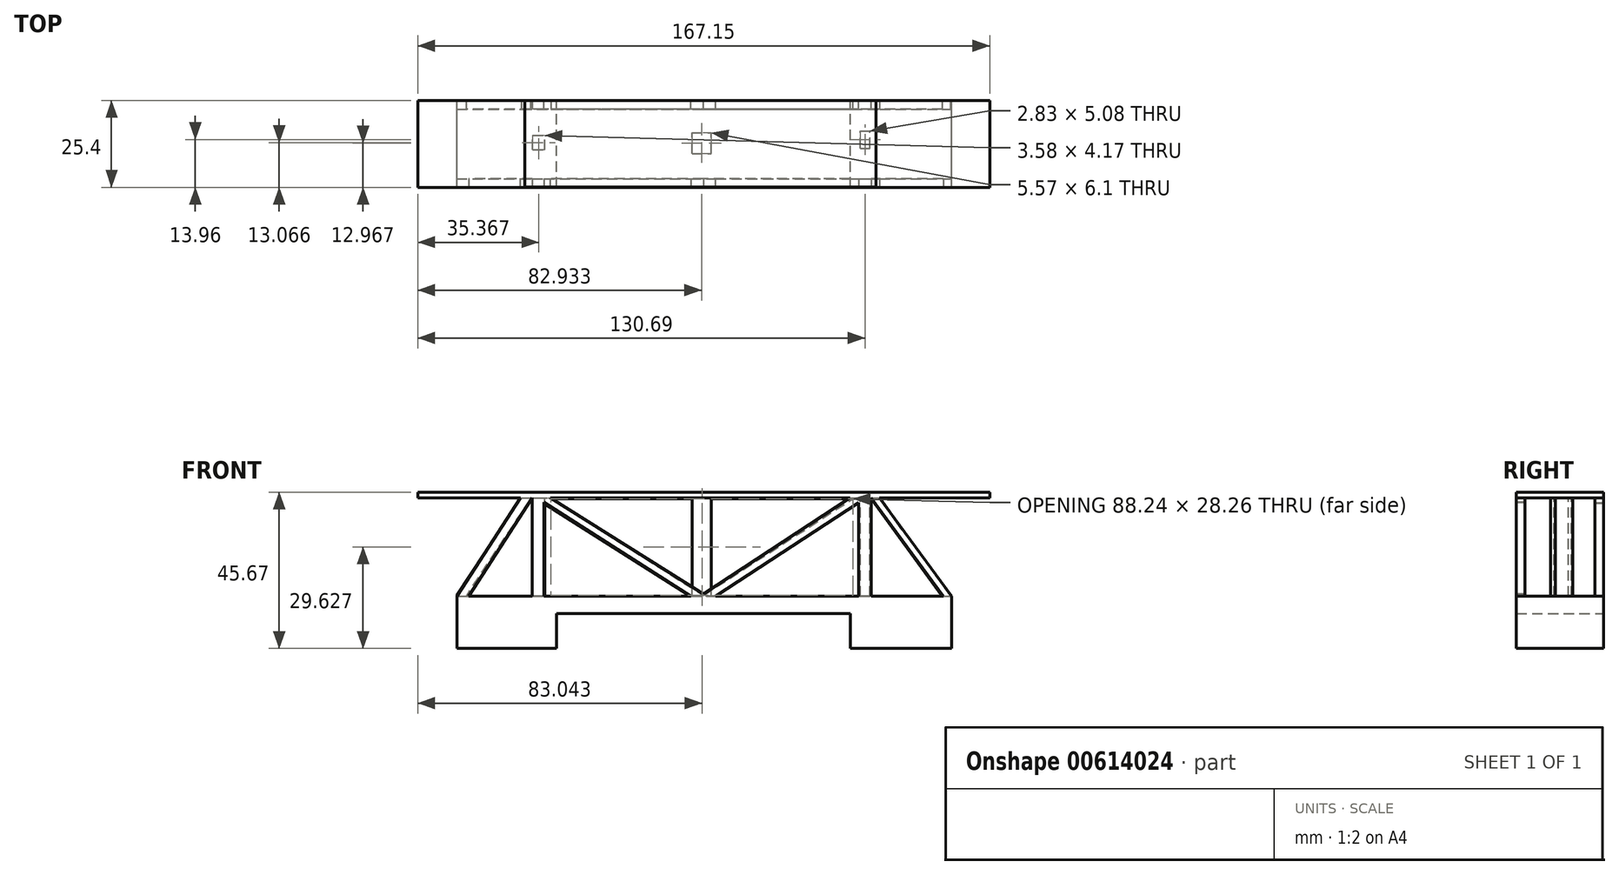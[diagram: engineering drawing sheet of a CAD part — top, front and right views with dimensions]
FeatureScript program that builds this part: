
annotation { "Feature Type Name" : "Feature", "Feature Type Description" : "" }
export const myFeature = defineFeature(function(context is Context, id is Id, definition is map)
    precondition{}
    {
        {
            var Q0;
            Q0=qCreatedBy(makeId("Front.planeOp"),FACE);
            var sketch = newSketch(context, id + "F0", { "sketchPlane" : qUnion([Q0])});
            skLineSegment(sketch, "E0.bottom", {"start": v(-72.04, 2.38) * mm, "end": v(72.6, 2.38) * mm});
            skLineSegment(sketch, "E0.top", {"start": v(-72.04, -2.66) * mm, "end": v(72.6, -2.66) * mm});
            skLineSegment(sketch, "E0.left", {"start": v(-72.04, 2.38) * mm, "end": v(-72.04, -2.66) * mm});
            skLineSegment(sketch, "E0.right", {"start": v(72.6, 2.38) * mm, "end": v(72.6, -2.66) * mm});
            skSolve(sketch);
        }
        {
            var Q0;
            Q0 = qSketchRegion(id + "F0", true);
            extrude(context, id + "F1", {"entities" : qUnion([Q0]), "depth" : 25.4 * mm, "offsetDistance" : 25.4 * mm});
        }
        {
            var Q0;
            Q0=qCreatedBy(makeId("Front.planeOp"),FACE);
            var sketch = newSketch(context, id + "F2", { "sketchPlane" : qUnion([Q0])});
            skLineSegment(sketch, "E1", {"start": v(-72.04, 0) * mm, "end": v(-72.04, 2.66) * mm});
            skLineSegment(sketch, "E2", {"start": v(-72.04, 2.66) * mm, "end": v(-52.17, 32.6) * mm});
            skLineSegment(sketch, "E3", {"start": v(-52.17, 32.6) * mm, "end": v(50.5, 32.6) * mm});
            skLineSegment(sketch, "E4", {"start": v(50.5, 32.6) * mm, "end": v(72.33, 2.35) * mm});
            skLineSegment(sketch, "E5", {"start": v(72.33, 2.35) * mm, "end": v(72.33, 0) * mm});
            skLineSegment(sketch, "E6", {"start": v(72.33, 0) * mm, "end": v(69.99, 0) * mm});
            skLineSegment(sketch, "E7", {"start": v(69.99, 0) * mm, "end": v(69.99, 2.13) * mm});
            skLineSegment(sketch, "E8", {"start": v(69.99, 2.13) * mm, "end": v(49, 30.94) * mm});
            skLineSegment(sketch, "E9", {"start": v(49, 30.94) * mm, "end": v(-50.44, 30.94) * mm});
            skLineSegment(sketch, "E10", {"start": v(-50.44, 30.94) * mm, "end": v(-69.24, 2.6) * mm});
            skLineSegment(sketch, "E11", {"start": v(-69.24, 2.6) * mm, "end": v(-69.24, 0) * mm});
            skLineSegment(sketch, "E12", {"start": v(-69.24, 0) * mm, "end": v(-72.04, 0) * mm});
            skSolve(sketch);
        }
        {
            var Q0;
            Q0 = qSketchRegion(id + "F2", true);
            extrude(context, id + "F3", {"entities" : qUnion([Q0]), "operationType" : NewBodyOperationType.ADD, "depth" : 2.54 * mm, "offsetDistance" : 25.4 * mm});
        }
        {
            var Q0;
            Q0=makeQuery(id+"F1.opExtrude","CAP_FACE",FACE,{"disambiguationData":[OSD([sQuery(id+"F0.wireOp",EDGE,"E0.bottom"),sQuery(id+"F0.wireOp",EDGE,"E0.top"),sQuery(id+"F0.wireOp",EDGE,"E0.left"),sQuery(id+"F0.wireOp",EDGE,"E0.right")])],"isStart":false});
            var sketch = newSketch(context, id + "F4", { "sketchPlane" : qUnion([Q0])});
            skLineSegment(sketch, "E13", {"start": v(-72.04, -0.14) * mm, "end": v(-72.04, 2.38) * mm});
            skLineSegment(sketch, "E14", {"start": v(-72.04, 2.38) * mm, "end": v(-52.32, 32.77) * mm});
            skLineSegment(sketch, "E15", {"start": v(-52.32, 32.77) * mm, "end": v(50.21, 32.77) * mm});
            skLineSegment(sketch, "E16", {"start": v(50.21, 32.77) * mm, "end": v(72.6, 2.38) * mm});
            skLineSegment(sketch, "E17", {"start": v(72.6, 2.38) * mm, "end": v(72.6, 0) * mm});
            skLineSegment(sketch, "E18", {"start": v(72.6, 0) * mm, "end": v(70.08, 0) * mm});
            skLineSegment(sketch, "E19", {"start": v(70.08, 0) * mm, "end": v(70.08, 2.38) * mm});
            skLineSegment(sketch, "E20", {"start": v(70.08, 2.38) * mm, "end": v(49.03, 31.08) * mm});
            skLineSegment(sketch, "E21", {"start": v(49.03, 31.08) * mm, "end": v(-49.96, 31.08) * mm});
            skLineSegment(sketch, "E22", {"start": v(-49.96, 31.08) * mm, "end": v(-68.59, 2.38) * mm});
            skLineSegment(sketch, "E23", {"start": v(-68.59, 2.38) * mm, "end": v(-68.59, 0) * mm});
            skLineSegment(sketch, "E24", {"start": v(-68.59, 0) * mm, "end": v(-72.04, -0.14) * mm});
            skSolve(sketch);
        }
        {
            var Q0;
            Q0 = qSketchRegion(id + "F4", true);
            extrude(context, id + "F5", {"entities" : qUnion([Q0]), "operationType" : NewBodyOperationType.ADD, "oppositeDirection" : true, "depth" : 2.54 * mm, "offsetDistance" : 25.4 * mm});
        }
        {
            var Q0;
            Q0=makeQuery(id+"F3.opExtrude","SWEPT_FACE",FACE,{"disambiguationData":[OSD([sQuery(id+"F2.wireOp",EDGE,"E3")])]});
            var sketch = newSketch(context, id + "F6", { "sketchPlane" : qUnion([Q0])});
            skLineSegment(sketch, "E25", {"start": v(-52.17, 0) * mm, "end": v(-52.17, -25.28) * mm});
            skLineSegment(sketch, "E26", {"start": v(-52.17, -25.28) * mm, "end": v(50.5, -25.28) * mm});
            skLineSegment(sketch, "E27", {"start": v(50.5, -25.28) * mm, "end": v(50.5, 0) * mm});
            skLineSegment(sketch, "E28", {"start": v(50.5, 0) * mm, "end": v(-52.17, 0) * mm});
            skSolve(sketch);
        }
        {
            var Q0;
            Q0 = qSketchRegion(id + "F6", true);
            extrude(context, id + "F7", {"entities" : qUnion([Q0]), "operationType" : NewBodyOperationType.ADD, "depth" : 0.25 * mm, "offsetDistance" : 25.4 * mm});
        }
        {
            var Q0;
            Q0=makeQuery(id+"F5.boolean.opBoolean","MERGE",FACE,{"derivedFrom":[makeQuery(id+"F1.opExtrude","CAP_FACE",FACE,{"disambiguationData":[OSD([sQuery(id+"F0.wireOp",EDGE,"E0.bottom"),sQuery(id+"F0.wireOp",EDGE,"E0.top"),sQuery(id+"F0.wireOp",EDGE,"E0.left"),sQuery(id+"F0.wireOp",EDGE,"E0.right")])],"isStart":false}),makeQuery(id+"F5.opExtrude","CAP_FACE",FACE,{"disambiguationData":[OSD([sQuery(id+"F4.wireOp",EDGE,"E13"),sQuery(id+"F4.wireOp",EDGE,"E14"),sQuery(id+"F4.wireOp",EDGE,"E15"),sQuery(id+"F4.wireOp",EDGE,"E16"),sQuery(id+"F4.wireOp",EDGE,"E17"),sQuery(id+"F4.wireOp",EDGE,"E18"),sQuery(id+"F4.wireOp",EDGE,"E19"),sQuery(id+"F4.wireOp",EDGE,"E20"),sQuery(id+"F4.wireOp",EDGE,"E21"),sQuery(id+"F4.wireOp",EDGE,"E22"),sQuery(id+"F4.wireOp",EDGE,"E23"),sQuery(id+"F4.wireOp",EDGE,"E24")])],"isStart":true})]});
            var sketch = newSketch(context, id + "F8", { "sketchPlane" : qUnion([Q0])});
            skLineSegment(sketch, "E29.bottom", {"start": v(-49.96, 31.99) * mm, "end": v(-46.53, 31.99) * mm});
            skLineSegment(sketch, "E29.top", {"start": v(-49.96, 1.21) * mm, "end": v(-46.53, 1.21) * mm});
            skLineSegment(sketch, "E29.left", {"start": v(-49.96, 31.99) * mm, "end": v(-49.96, 1.21) * mm});
            skLineSegment(sketch, "E29.right", {"start": v(-46.53, 31.99) * mm, "end": v(-46.53, 1.21) * mm});
            skSolve(sketch);
        }
        {
            var Q0;
            Q0 = qSketchRegion(id + "F8", true);
            extrude(context, id + "F9", {"entities" : qUnion([Q0]), "operationType" : NewBodyOperationType.ADD, "oppositeDirection" : true, "depth" : 2.54 * mm, "offsetDistance" : 25.4 * mm});
        }
        {
            var Q0;
            Q0=makeQuery(id+"F9.boolean.opBoolean","MERGE",FACE,{"derivedFrom":[makeQuery(id+"F5.boolean.opBoolean","MERGE",FACE,{"derivedFrom":[makeQuery(id+"F1.opExtrude","CAP_FACE",FACE,{"disambiguationData":[OSD([sQuery(id+"F0.wireOp",EDGE,"E0.bottom"),sQuery(id+"F0.wireOp",EDGE,"E0.top"),sQuery(id+"F0.wireOp",EDGE,"E0.left"),sQuery(id+"F0.wireOp",EDGE,"E0.right")])],"isStart":false}),makeQuery(id+"F5.opExtrude","CAP_FACE",FACE,{"disambiguationData":[OSD([sQuery(id+"F4.wireOp",EDGE,"E13"),sQuery(id+"F4.wireOp",EDGE,"E14"),sQuery(id+"F4.wireOp",EDGE,"E15"),sQuery(id+"F4.wireOp",EDGE,"E16"),sQuery(id+"F4.wireOp",EDGE,"E17"),sQuery(id+"F4.wireOp",EDGE,"E18"),sQuery(id+"F4.wireOp",EDGE,"E19"),sQuery(id+"F4.wireOp",EDGE,"E20"),sQuery(id+"F4.wireOp",EDGE,"E21"),sQuery(id+"F4.wireOp",EDGE,"E22"),sQuery(id+"F4.wireOp",EDGE,"E23"),sQuery(id+"F4.wireOp",EDGE,"E24")])],"isStart":true})]}),makeQuery(id+"F9.opExtrude","CAP_FACE",FACE,{"disambiguationData":[OSD([sQuery(id+"F8.wireOp",EDGE,"E29.bottom"),sQuery(id+"F8.wireOp",EDGE,"E29.top"),sQuery(id+"F8.wireOp",EDGE,"E29.left"),sQuery(id+"F8.wireOp",EDGE,"E29.right")])],"isStart":true})]});
            var sketch = newSketch(context, id + "F10", { "sketchPlane" : qUnion([Q0])});
            skLineSegment(sketch, "E30.bottom", {"start": v(49.03, 32.15) * mm, "end": v(45.4, 32.15) * mm});
            skLineSegment(sketch, "E30.top", {"start": v(49.03, 0) * mm, "end": v(45.4, 0) * mm});
            skLineSegment(sketch, "E30.left", {"start": v(49.03, 32.15) * mm, "end": v(49.03, 0) * mm});
            skLineSegment(sketch, "E30.right", {"start": v(45.4, 32.15) * mm, "end": v(45.4, 0) * mm});
            skSolve(sketch);
        }
        {
            var Q0;
            Q0 = qSketchRegion(id + "F10", true);
            extrude(context, id + "F11", {"entities" : qUnion([Q0]), "operationType" : NewBodyOperationType.ADD, "oppositeDirection" : true, "depth" : 2.54 * mm, "offsetDistance" : 25.4 * mm});
        }
        {
            var Q0;
            Q0=makeQuery(id+"F7.boolean.opBoolean","MERGE",FACE,{"derivedFrom":[makeQuery(id+"F3.boolean.opBoolean","MERGE",FACE,{"derivedFrom":[makeQuery(id+"F1.opExtrude","CAP_FACE",FACE,{"disambiguationData":[OSD([sQuery(id+"F0.wireOp",EDGE,"E0.bottom"),sQuery(id+"F0.wireOp",EDGE,"E0.top"),sQuery(id+"F0.wireOp",EDGE,"E0.left"),sQuery(id+"F0.wireOp",EDGE,"E0.right")])],"isStart":true}),makeQuery(id+"F3.opExtrude","CAP_FACE",FACE,{"disambiguationData":[OSD([sQuery(id+"F2.wireOp",EDGE,"E1"),sQuery(id+"F2.wireOp",EDGE,"E2"),sQuery(id+"F2.wireOp",EDGE,"E3"),sQuery(id+"F2.wireOp",EDGE,"E4"),sQuery(id+"F2.wireOp",EDGE,"E5"),sQuery(id+"F2.wireOp",EDGE,"E6"),sQuery(id+"F2.wireOp",EDGE,"E7"),sQuery(id+"F2.wireOp",EDGE,"E8"),sQuery(id+"F2.wireOp",EDGE,"E9"),sQuery(id+"F2.wireOp",EDGE,"E10"),sQuery(id+"F2.wireOp",EDGE,"E11"),sQuery(id+"F2.wireOp",EDGE,"E12")])],"isStart":true})]}),makeQuery(id+"F7.opExtrude","SWEPT_FACE",FACE,{"disambiguationData":[OSD([sQuery(id+"F6.wireOp",EDGE,"E28")])]})]});
            var sketch = newSketch(context, id + "F12", { "sketchPlane" : qUnion([Q0])});
            skLineSegment(sketch, "E31.bottom", {"start": v(-49, 31.88) * mm, "end": v(-45.36, 31.88) * mm});
            skLineSegment(sketch, "E31.top", {"start": v(-49, 0.91) * mm, "end": v(-45.36, 0.91) * mm});
            skLineSegment(sketch, "E31.left", {"start": v(-49, 31.88) * mm, "end": v(-49, 0.91) * mm});
            skLineSegment(sketch, "E31.right", {"start": v(-45.36, 31.88) * mm, "end": v(-45.36, 0.91) * mm});
            skSolve(sketch);
        }
        {
            var Q0;
            Q0 = qSketchRegion(id + "F12", true);
            extrude(context, id + "F13", {"entities" : qUnion([Q0]), "operationType" : NewBodyOperationType.ADD, "oppositeDirection" : true, "depth" : 2.54 * mm, "offsetDistance" : 25.4 * mm});
        }
        {
            var Q0;
            Q0=makeQuery(id+"F13.boolean.opBoolean","MERGE",FACE,{"derivedFrom":[makeQuery(id+"F7.boolean.opBoolean","MERGE",FACE,{"derivedFrom":[makeQuery(id+"F3.boolean.opBoolean","MERGE",FACE,{"derivedFrom":[makeQuery(id+"F1.opExtrude","CAP_FACE",FACE,{"disambiguationData":[OSD([sQuery(id+"F0.wireOp",EDGE,"E0.bottom"),sQuery(id+"F0.wireOp",EDGE,"E0.top"),sQuery(id+"F0.wireOp",EDGE,"E0.left"),sQuery(id+"F0.wireOp",EDGE,"E0.right")])],"isStart":true}),makeQuery(id+"F3.opExtrude","CAP_FACE",FACE,{"disambiguationData":[OSD([sQuery(id+"F2.wireOp",EDGE,"E1"),sQuery(id+"F2.wireOp",EDGE,"E2"),sQuery(id+"F2.wireOp",EDGE,"E3"),sQuery(id+"F2.wireOp",EDGE,"E4"),sQuery(id+"F2.wireOp",EDGE,"E5"),sQuery(id+"F2.wireOp",EDGE,"E6"),sQuery(id+"F2.wireOp",EDGE,"E7"),sQuery(id+"F2.wireOp",EDGE,"E8"),sQuery(id+"F2.wireOp",EDGE,"E9"),sQuery(id+"F2.wireOp",EDGE,"E10"),sQuery(id+"F2.wireOp",EDGE,"E11"),sQuery(id+"F2.wireOp",EDGE,"E12")])],"isStart":true})]}),makeQuery(id+"F7.opExtrude","SWEPT_FACE",FACE,{"disambiguationData":[OSD([sQuery(id+"F6.wireOp",EDGE,"E28")])]})]}),makeQuery(id+"F13.opExtrude","CAP_FACE",FACE,{"disambiguationData":[OSD([sQuery(id+"F12.wireOp",EDGE,"E31.bottom"),sQuery(id+"F12.wireOp",EDGE,"E31.top"),sQuery(id+"F12.wireOp",EDGE,"E31.left"),sQuery(id+"F12.wireOp",EDGE,"E31.right")])],"isStart":true})]});
            var sketch = newSketch(context, id + "F14", { "sketchPlane" : qUnion([Q0])});
            skLineSegment(sketch, "E32.bottom", {"start": v(46.58, 31.88) * mm, "end": v(50.04, 31.88) * mm});
            skLineSegment(sketch, "E32.top", {"start": v(46.58, 1.46) * mm, "end": v(50.04, 1.46) * mm});
            skLineSegment(sketch, "E32.left", {"start": v(46.58, 31.88) * mm, "end": v(46.58, 1.46) * mm});
            skLineSegment(sketch, "E32.right", {"start": v(50.04, 31.88) * mm, "end": v(50.04, 1.46) * mm});
            skSolve(sketch);
        }
        {
            var Q0;
            Q0 = qSketchRegion(id + "F14", true);
            extrude(context, id + "F15", {"entities" : qUnion([Q0]), "operationType" : NewBodyOperationType.ADD, "oppositeDirection" : true, "depth" : 2.54 * mm, "offsetDistance" : 25.4 * mm});
        }
        {
            var Q0;
            Q0=makeQuery(id+"F15.boolean.opBoolean","MERGE",FACE,{"derivedFrom":[makeQuery(id+"F13.boolean.opBoolean","MERGE",FACE,{"derivedFrom":[makeQuery(id+"F7.boolean.opBoolean","MERGE",FACE,{"derivedFrom":[makeQuery(id+"F3.boolean.opBoolean","MERGE",FACE,{"derivedFrom":[makeQuery(id+"F1.opExtrude","CAP_FACE",FACE,{"disambiguationData":[OSD([sQuery(id+"F0.wireOp",EDGE,"E0.bottom"),sQuery(id+"F0.wireOp",EDGE,"E0.top"),sQuery(id+"F0.wireOp",EDGE,"E0.left"),sQuery(id+"F0.wireOp",EDGE,"E0.right")])],"isStart":true}),makeQuery(id+"F3.opExtrude","CAP_FACE",FACE,{"disambiguationData":[OSD([sQuery(id+"F2.wireOp",EDGE,"E1"),sQuery(id+"F2.wireOp",EDGE,"E2"),sQuery(id+"F2.wireOp",EDGE,"E3"),sQuery(id+"F2.wireOp",EDGE,"E4"),sQuery(id+"F2.wireOp",EDGE,"E5"),sQuery(id+"F2.wireOp",EDGE,"E6"),sQuery(id+"F2.wireOp",EDGE,"E7"),sQuery(id+"F2.wireOp",EDGE,"E8"),sQuery(id+"F2.wireOp",EDGE,"E9"),sQuery(id+"F2.wireOp",EDGE,"E10"),sQuery(id+"F2.wireOp",EDGE,"E11"),sQuery(id+"F2.wireOp",EDGE,"E12")])],"isStart":true})]}),makeQuery(id+"F7.opExtrude","SWEPT_FACE",FACE,{"disambiguationData":[OSD([sQuery(id+"F6.wireOp",EDGE,"E28")])]})]}),makeQuery(id+"F13.opExtrude","CAP_FACE",FACE,{"disambiguationData":[OSD([sQuery(id+"F12.wireOp",EDGE,"E31.bottom"),sQuery(id+"F12.wireOp",EDGE,"E31.top"),sQuery(id+"F12.wireOp",EDGE,"E31.left"),sQuery(id+"F12.wireOp",EDGE,"E31.right")])],"isStart":true})]}),makeQuery(id+"F15.opExtrude","CAP_FACE",FACE,{"disambiguationData":[OSD([sQuery(id+"F14.wireOp",EDGE,"E32.bottom"),sQuery(id+"F14.wireOp",EDGE,"E32.top"),sQuery(id+"F14.wireOp",EDGE,"E32.left"),sQuery(id+"F14.wireOp",EDGE,"E32.right")])],"isStart":true})]});
            var sketch = newSketch(context, id + "F16", { "sketchPlane" : qUnion([Q0])});
            skLineSegment(sketch, "E33", {"start": v(-47.16, 30.94) * mm, "end": v(0, 0) * mm});
            skLineSegment(sketch, "E34", {"start": v(0, 0) * mm, "end": v(48.75, 30.94) * mm});
            skLineSegment(sketch, "E35", {"start": v(48.75, 30.94) * mm, "end": v(47.54, 32.85) * mm});
            skLineSegment(sketch, "E36", {"start": v(47.54, 32.85) * mm, "end": v(0, 2.68) * mm});
            skLineSegment(sketch, "E37", {"start": v(0, 2.68) * mm, "end": v(-45.36, 32) * mm});
            skLineSegment(sketch, "E38", {"start": v(-45.36, 32) * mm, "end": v(-47.16, 30.94) * mm});
            skSolve(sketch);
        }
        {
            var Q0;
            Q0 = qSketchRegion(id + "F16", true);
            extrude(context, id + "F17", {"entities" : qUnion([Q0]), "operationType" : NewBodyOperationType.ADD, "oppositeDirection" : true, "depth" : 2.54 * mm, "offsetDistance" : 25.4 * mm});
        }
        {
            var Q0;
            Q0=makeQuery(id+"F11.boolean.opBoolean","MERGE",FACE,{"derivedFrom":[makeQuery(id+"F9.boolean.opBoolean","MERGE",FACE,{"derivedFrom":[makeQuery(id+"F5.boolean.opBoolean","MERGE",FACE,{"derivedFrom":[makeQuery(id+"F1.opExtrude","CAP_FACE",FACE,{"disambiguationData":[OSD([sQuery(id+"F0.wireOp",EDGE,"E0.bottom"),sQuery(id+"F0.wireOp",EDGE,"E0.top"),sQuery(id+"F0.wireOp",EDGE,"E0.left"),sQuery(id+"F0.wireOp",EDGE,"E0.right")])],"isStart":false}),makeQuery(id+"F5.opExtrude","CAP_FACE",FACE,{"disambiguationData":[OSD([sQuery(id+"F4.wireOp",EDGE,"E13"),sQuery(id+"F4.wireOp",EDGE,"E14"),sQuery(id+"F4.wireOp",EDGE,"E15"),sQuery(id+"F4.wireOp",EDGE,"E16"),sQuery(id+"F4.wireOp",EDGE,"E17"),sQuery(id+"F4.wireOp",EDGE,"E18"),sQuery(id+"F4.wireOp",EDGE,"E19"),sQuery(id+"F4.wireOp",EDGE,"E20"),sQuery(id+"F4.wireOp",EDGE,"E21"),sQuery(id+"F4.wireOp",EDGE,"E22"),sQuery(id+"F4.wireOp",EDGE,"E23"),sQuery(id+"F4.wireOp",EDGE,"E24")])],"isStart":true})]}),makeQuery(id+"F9.opExtrude","CAP_FACE",FACE,{"disambiguationData":[OSD([sQuery(id+"F8.wireOp",EDGE,"E29.bottom"),sQuery(id+"F8.wireOp",EDGE,"E29.top"),sQuery(id+"F8.wireOp",EDGE,"E29.left"),sQuery(id+"F8.wireOp",EDGE,"E29.right")])],"isStart":true})]}),makeQuery(id+"F11.opExtrude","CAP_FACE",FACE,{"disambiguationData":[OSD([sQuery(id+"F10.wireOp",EDGE,"E30.bottom"),sQuery(id+"F10.wireOp",EDGE,"E30.top"),sQuery(id+"F10.wireOp",EDGE,"E30.left"),sQuery(id+"F10.wireOp",EDGE,"E30.right")])],"isStart":true})]});
            var sketch = newSketch(context, id + "F18", { "sketchPlane" : qUnion([Q0])});
            skLineSegment(sketch, "E39", {"start": v(-48.43, 31.08) * mm, "end": v(0, 0) * mm});
            skLineSegment(sketch, "E40", {"start": v(0, 0) * mm, "end": v(47.51, 31.08) * mm});
            skLineSegment(sketch, "E41", {"start": v(47.51, 31.08) * mm, "end": v(45.4, 32.77) * mm});
            skLineSegment(sketch, "E42", {"start": v(45.4, 32.77) * mm, "end": v(0, 3.06) * mm});
            skLineSegment(sketch, "E43", {"start": v(0, 3.06) * mm, "end": v(-46.53, 32.24) * mm});
            skLineSegment(sketch, "E44", {"start": v(-46.53, 32.24) * mm, "end": v(-48.43, 31.08) * mm});
            skSolve(sketch);
        }
        {
            var Q0;
            Q0 = qSketchRegion(id + "F18", true);
            extrude(context, id + "F19", {"entities" : qUnion([Q0]), "operationType" : NewBodyOperationType.ADD, "oppositeDirection" : true, "depth" : 2.54 * mm, "offsetDistance" : 25.4 * mm});
        }
        {
            var Q0;
            Q0=makeQuery(id+"F7.opExtrude","CAP_FACE",FACE,{"disambiguationData":[OSD([sQuery(id+"F6.wireOp",EDGE,"E25"),sQuery(id+"F6.wireOp",EDGE,"E26"),sQuery(id+"F6.wireOp",EDGE,"E27"),sQuery(id+"F6.wireOp",EDGE,"E28")])],"isStart":true});
            var sketch = newSketch(context, id + "F20", { "sketchPlane" : qUnion([Q0])});
            skLineSegment(sketch, "E45.bottom", {"start": v(-3.3, 15.48) * mm, "end": v(2.27, 15.48) * mm});
            skLineSegment(sketch, "E45.top", {"start": v(-3.3, 9.38) * mm, "end": v(2.27, 9.38) * mm});
            skLineSegment(sketch, "E45.left", {"start": v(-3.3, 15.48) * mm, "end": v(-3.3, 9.38) * mm});
            skLineSegment(sketch, "E45.right", {"start": v(2.27, 15.48) * mm, "end": v(2.27, 9.38) * mm});
            skSolve(sketch);
        }
        {
            var Q0;
            Q0 = qSketchRegion(id + "F20", true);
            extrude(context, id + "F21", {"entities" : qUnion([Q0]), "operationType" : NewBodyOperationType.ADD, "depth" : 33.02 * mm, "offsetDistance" : 25.4 * mm});
        }
        {
            var Q0;
            Q0=makeQuery(id+"F7.opExtrude","CAP_FACE",FACE,{"disambiguationData":[OSD([sQuery(id+"F6.wireOp",EDGE,"E25"),sQuery(id+"F6.wireOp",EDGE,"E26"),sQuery(id+"F6.wireOp",EDGE,"E27"),sQuery(id+"F6.wireOp",EDGE,"E28")])],"isStart":true});
            var sketch = newSketch(context, id + "F22", { "sketchPlane" : qUnion([Q0])});
            skLineSegment(sketch, "E46.bottom", {"start": v(-49.87, 14.42) * mm, "end": v(-46.3, 14.42) * mm});
            skLineSegment(sketch, "E46.top", {"start": v(-49.87, 10.25) * mm, "end": v(-46.3, 10.25) * mm});
            skLineSegment(sketch, "E46.left", {"start": v(-49.87, 14.42) * mm, "end": v(-49.87, 10.25) * mm});
            skLineSegment(sketch, "E46.right", {"start": v(-46.3, 14.42) * mm, "end": v(-46.3, 10.25) * mm});
            skSolve(sketch);
        }
        {
            var Q0;
            Q0 = qSketchRegion(id + "F22", true);
            extrude(context, id + "F23", {"entities" : qUnion([Q0]), "operationType" : NewBodyOperationType.ADD, "depth" : 33.02 * mm, "offsetDistance" : 25.4 * mm});
        }
        {
            var Q0;
            Q0=makeQuery(id+"F7.opExtrude","CAP_FACE",FACE,{"disambiguationData":[OSD([sQuery(id+"F6.wireOp",EDGE,"E25"),sQuery(id+"F6.wireOp",EDGE,"E26"),sQuery(id+"F6.wireOp",EDGE,"E27"),sQuery(id+"F6.wireOp",EDGE,"E28")])],"isStart":true});
            var sketch = newSketch(context, id + "F24", { "sketchPlane" : qUnion([Q0])});
            skLineSegment(sketch, "E47.bottom", {"start": v(45.82, 13.98) * mm, "end": v(48.66, 13.98) * mm});
            skLineSegment(sketch, "E47.top", {"start": v(45.82, 8.9) * mm, "end": v(48.66, 8.9) * mm});
            skLineSegment(sketch, "E47.left", {"start": v(45.82, 13.98) * mm, "end": v(45.82, 8.9) * mm});
            skLineSegment(sketch, "E47.right", {"start": v(48.66, 13.98) * mm, "end": v(48.66, 8.9) * mm});
            skSolve(sketch);
        }
        {
            var Q0;
            Q0 = qSketchRegion(id + "F24", true);
            extrude(context, id + "F25", {"entities" : qUnion([Q0]), "operationType" : NewBodyOperationType.ADD, "depth" : 33.02 * mm, "offsetDistance" : 25.4 * mm});
        }
        {
            var Q0;
            Q0=makeQuery(id+"F19.boolean.opBoolean","MERGE",FACE,{"derivedFrom":[makeQuery(id+"F11.boolean.opBoolean","MERGE",FACE,{"derivedFrom":[makeQuery(id+"F9.boolean.opBoolean","MERGE",FACE,{"derivedFrom":[makeQuery(id+"F5.boolean.opBoolean","MERGE",FACE,{"derivedFrom":[makeQuery(id+"F1.opExtrude","CAP_FACE",FACE,{"disambiguationData":[OSD([sQuery(id+"F0.wireOp",EDGE,"E0.bottom"),sQuery(id+"F0.wireOp",EDGE,"E0.top"),sQuery(id+"F0.wireOp",EDGE,"E0.left"),sQuery(id+"F0.wireOp",EDGE,"E0.right")])],"isStart":false}),makeQuery(id+"F5.opExtrude","CAP_FACE",FACE,{"disambiguationData":[OSD([sQuery(id+"F4.wireOp",EDGE,"E13"),sQuery(id+"F4.wireOp",EDGE,"E14"),sQuery(id+"F4.wireOp",EDGE,"E15"),sQuery(id+"F4.wireOp",EDGE,"E16"),sQuery(id+"F4.wireOp",EDGE,"E17"),sQuery(id+"F4.wireOp",EDGE,"E18"),sQuery(id+"F4.wireOp",EDGE,"E19"),sQuery(id+"F4.wireOp",EDGE,"E20"),sQuery(id+"F4.wireOp",EDGE,"E21"),sQuery(id+"F4.wireOp",EDGE,"E22"),sQuery(id+"F4.wireOp",EDGE,"E23"),sQuery(id+"F4.wireOp",EDGE,"E24")])],"isStart":true})]}),makeQuery(id+"F9.opExtrude","CAP_FACE",FACE,{"disambiguationData":[OSD([sQuery(id+"F8.wireOp",EDGE,"E29.bottom"),sQuery(id+"F8.wireOp",EDGE,"E29.top"),sQuery(id+"F8.wireOp",EDGE,"E29.left"),sQuery(id+"F8.wireOp",EDGE,"E29.right")])],"isStart":true})]}),makeQuery(id+"F11.opExtrude","CAP_FACE",FACE,{"disambiguationData":[OSD([sQuery(id+"F10.wireOp",EDGE,"E30.bottom"),sQuery(id+"F10.wireOp",EDGE,"E30.top"),sQuery(id+"F10.wireOp",EDGE,"E30.left"),sQuery(id+"F10.wireOp",EDGE,"E30.right")])],"isStart":true})]}),makeQuery(id+"F19.opExtrude","CAP_FACE",FACE,{"disambiguationData":[OSD([sQuery(id+"F18.wireOp",EDGE,"E39"),sQuery(id+"F18.wireOp",EDGE,"E40"),sQuery(id+"F18.wireOp",EDGE,"E41"),sQuery(id+"F18.wireOp",EDGE,"E42"),sQuery(id+"F18.wireOp",EDGE,"E43"),sQuery(id+"F18.wireOp",EDGE,"E44")])],"isStart":true})]});
            var sketch = newSketch(context, id + "F26", { "sketchPlane" : qUnion([Q0])});
            skLineSegment(sketch, "E48.bottom", {"start": v(-83.45, 32.77) * mm, "end": v(83.7, 32.77) * mm});
            skLineSegment(sketch, "E48.top", {"start": v(-83.45, 31.08) * mm, "end": v(83.7, 31.08) * mm});
            skLineSegment(sketch, "E48.left", {"start": v(-83.45, 32.77) * mm, "end": v(-83.45, 31.08) * mm});
            skLineSegment(sketch, "E48.right", {"start": v(83.7, 32.77) * mm, "end": v(83.7, 31.08) * mm});
            skSolve(sketch);
        }
        {
            var Q0;
            Q0 = qSketchRegion(id + "F26", true);
            extrude(context, id + "F27", {"entities" : qUnion([Q0]), "operationType" : NewBodyOperationType.ADD, "oppositeDirection" : true, "depth" : 25.4 * mm, "offsetDistance" : 25.4 * mm});
        }
        {
            var Q0;
            Q0=makeQuery(id+"F1.opExtrude","SWEPT_FACE",FACE,{"disambiguationData":[OSD([sQuery(id+"F0.wireOp",EDGE,"E0.top")])]});
            var sketch = newSketch(context, id + "F28", { "sketchPlane" : qUnion([Q0])});
            skLineSegment(sketch, "E49.bottom", {"start": v(-72.04, 25.4) * mm, "end": v(-42.9, 25.4) * mm});
            skLineSegment(sketch, "E49.top", {"start": v(-72.04, 0) * mm, "end": v(-42.9, 0) * mm});
            skLineSegment(sketch, "E49.left", {"start": v(-72.04, 25.4) * mm, "end": v(-72.04, 0) * mm});
            skLineSegment(sketch, "E49.right", {"start": v(-42.9, 25.4) * mm, "end": v(-42.9, 0) * mm});
            skSolve(sketch);
        }
        {
            var Q0;
            Q0 = qSketchRegion(id + "F28", true);
            extrude(context, id + "F29", {"entities" : qUnion([Q0]), "operationType" : NewBodyOperationType.ADD, "depth" : 10.16 * mm, "offsetDistance" : 25.4 * mm});
        }
        {
            var Q0;
            Q0=makeQuery(id+"F1.opExtrude","SWEPT_FACE",FACE,{"disambiguationData":[OSD([sQuery(id+"F0.wireOp",EDGE,"E0.top")])]});
            var sketch = newSketch(context, id + "F30", { "sketchPlane" : qUnion([Q0])});
            skLineSegment(sketch, "E50.bottom", {"start": v(72.6, 25.4) * mm, "end": v(42.98, 25.4) * mm});
            skLineSegment(sketch, "E50.top", {"start": v(72.6, 0) * mm, "end": v(42.98, 0) * mm});
            skLineSegment(sketch, "E50.left", {"start": v(72.6, 25.4) * mm, "end": v(72.6, 0) * mm});
            skLineSegment(sketch, "E50.right", {"start": v(42.98, 25.4) * mm, "end": v(42.98, 0) * mm});
            skSolve(sketch);
        }
        {
            var Q0;
            Q0 = qSketchRegion(id + "F30", true);
            extrude(context, id + "F31", {"entities" : qUnion([Q0]), "operationType" : NewBodyOperationType.ADD, "depth" : 10.16 * mm, "offsetDistance" : 25.4 * mm});
        }
    });
